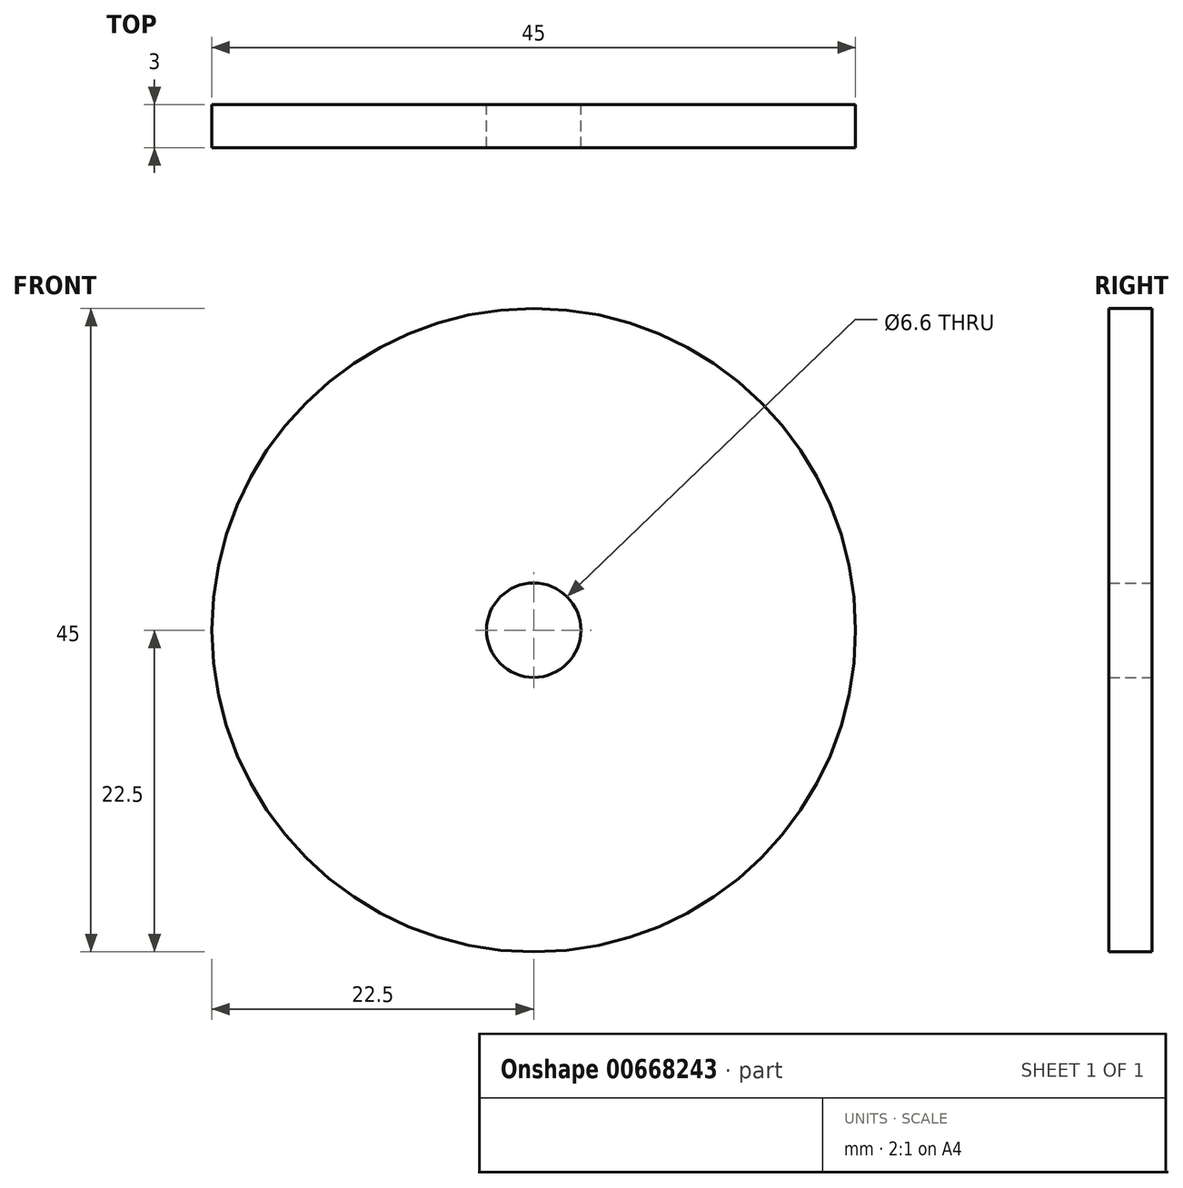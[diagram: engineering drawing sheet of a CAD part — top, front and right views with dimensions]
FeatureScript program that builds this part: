
annotation { "Feature Type Name" : "Feature", "Feature Type Description" : "" }
export const myFeature = defineFeature(function(context is Context, id is Id, definition is map)
    precondition{}
    {
        {
            var Q0;
            Q0=qCreatedBy(makeId("Front.planeOp"),FACE);
            var sketch = newSketch(context, id + "F0", { "sketchPlane" : qUnion([Q0])});
            skCircle(sketch, "E0", {"center": v(0, 0) * mm, "radius": 22.5 * mm});
            skCircle(sketch, "E1", {"center": v(0, 0) * mm, "radius": 3.3 * mm});
            skSolve(sketch);
        }
        {
            var Q0;
            Q0=qSketchRegion(id+"F0",true);
            extrude(context, id + "F1", {"entities" : qUnion([Q0]), "depth" : 3 * mm, "offsetDistance" : 25 * mm});
        }
    });
